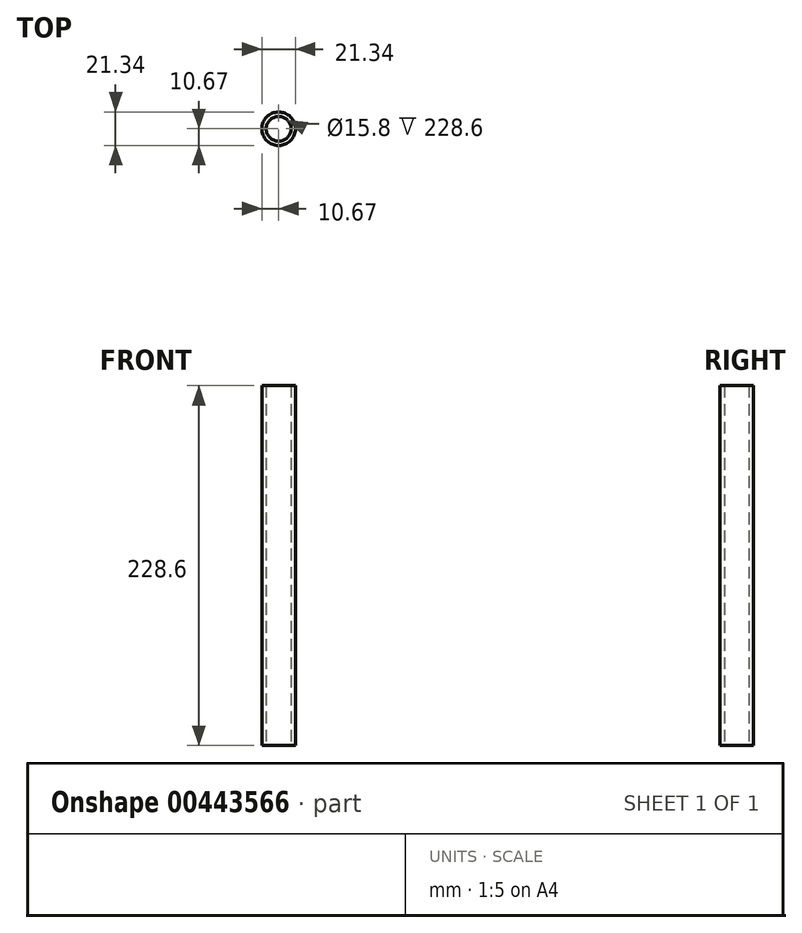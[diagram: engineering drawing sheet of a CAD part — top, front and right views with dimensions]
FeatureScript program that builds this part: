
annotation { "Feature Type Name" : "Feature", "Feature Type Description" : "" }
export const myFeature = defineFeature(function(context is Context, id is Id, definition is map)
    precondition{}
    {
        {
            var Q0;
            Q0=qCreatedBy(makeId("Top.planeOp"),FACE);
            var sketch = newSketch(context, id + "F0", { "sketchPlane" : qUnion([Q0])});
            skCircle(sketch, "E0", {"center": v(0, 0) * mm, "radius": 10.67 * mm});
            skCircle(sketch, "E1", {"center": v(0, 0) * mm, "radius": 7.9 * mm});
            skSolve(sketch);
        }
        {
            var Q0;
            Q0 = qSketchRegion(id + "F0", true);
            extrude(context, id + "F1", {"entities" : qUnion([Q0]), "depth" : 228.6 * mm});
        }
    });
